# Revit family: IS_Iom_A9120_BIM_DE
name_source: partatom
category: Plumbing Fixtures
revit_build: Autodesk Revit MEP 2016 (Build: 20161004_0715(x64)
units: mm (PartAtom-declared; Revit-internal decimal feet)

## family parameters
Always vertical = No
Cut with Voids When Loaded = No
OmniClass Number = 23.45.05.14.21.11
OmniClass Title = Bath/Shower Units
Part Type = Normal
Room Calculation Point = No
Round Connector Dimension = Use Diameter
Shared = No
Work Plane-Based = No

## types (1)
- A9120AA IOM tumbler
    Accessories = www.idealstandard.de\ersatzteile
    AssetType = Fixed
    BIMObjectName = ISI_IdealStandard_TumblerHolders_Iom_A9120AA
    BIMobject category = Accessories
    BOSUseNativeGeometries = 1
    BarCode = 4015413327947
    Brand = Ideal Standard
    Brand url = http://www.idealstandard.de
    CodePerformance = 0
    Color = Chrome
    ConnectionType = Plumbing
    Cost = 0 $
    CurrencyUnit = €
    CurrentRevision = 1
    Date of publishing = 20/12/2017
    Description = IS Zahnbecher IOM aus satiniertem Glas Chrom
    DurationUnit = Year
    EAN code = https://4015413327947
    Edition number = 1
    ExpectedLife = 25
    Features = IS Zahnbecher IOM aus satiniertem Glas Chrom
    Finish = Chrome
    IFC Classification = Sanitary Terminal
    IfcExportAs = IfcSanitaryTerminalType
    Installation instructions = http://www.idealstandard.de
    InstallationInstructions = www.idealstandard.de\produkte
    MainColor = Chrome
    MaintenanceInformation = www.idealstandard.de\produkte
    Manufacturer name = Ideal Standard
    ManufacturerURL = http://www.idealstandard.de
    Material = 0
    Model = A9120AA
    ModelNumber = A9120AA
    ModelReference = IS Zahnbecher IOM aus satiniertem Glas Chrom
    NBS Reference Code = 35-75-92
    NBS Reference Description = Tumbler Holders
    Name = TumblerHolders_Iom_A9120AA
    NettWeight = 0.38 Kg
    Nominal height = 96
    Nominal width = 66
    NominalDepth = 105 mm  [stored 0.344488 ft]
    NominalHeight = 96 mm  [stored 0.314961 ft]
    NominalLength = 105 mm  [stored 0.344488 ft]
    NominalWidth = 69 mm  [stored 0.226378 ft]
    OmniClass Code = 23-31 25 00
    OmniClass Description = Toilet and Bath Specialties
    Product Guid = 28893b59-718d-4b35-904c-dda71c4f0fe6
    Product SKU = A9120
    Product data url = https://bimobject.com
    Product family = Sanitary
    Product group = Accessories
    Product name = IOM tumbler
    Product url = http://www.idealstandard.de
    ProductInformation = www.idealstandard.de/produkte
    QR code = http://bimobject.com
    Shape = Sculptured
    Size = 69x105x96 mm
    Space = Internal
    SpareParts = www.idealstandard.de/ersatzteile
    Technical description = http://www.idealstandard.de
    URL = http://www.idealstandard.de
    Uniclass 1.4 Code = L7313
    Uniclass 1.4 Description = Sanitary above ground pipes and fittings
    Uniclass 2.0 Code = PR-35-75-92
    Uniclass 2.0 Description = Tumbler Holders
    Uniclass 2015 Code = Pr_40_20_76_92
    Uniclass 2015 Name = Tumbler holders
    Uniclass2015Code = Pr_40_20_76_92
    Uniclass2015Title = Tumbler holders
    Uniclass2015Version = Products v1.1
    Version = 1
    VolumeUnits = Litres
    Weight Net (Kg) = 0.38

note: [stored X ft] marks values corroborated as IEEE doubles in the binary element streams (Revit-internal decimal feet)

## geometry (parser evidence)
native form markers: Blend x2, Sweep x3
no freeform markers — native parametric forms only
